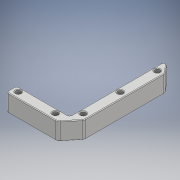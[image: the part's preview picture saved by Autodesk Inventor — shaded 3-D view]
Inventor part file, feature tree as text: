
AUTODESK INVENTOR PART (.ipt)
format: ipt  version: 2018 (Build 220112000, 112)  size: 404,992 bytes
history: native  units: mm
features: extrude x1, fillet x1, sketch x1
ambient origin geometry x8: Origin, YZ Plane, XZ Plane, XY Plane, X Axis, Y Axis, Z Axis, Center Point
bodies: Solid1 (feature_tree)
feature tree (3):
  extrude  "Extrusion1"  Depth=0.3mm
  fillet  "Fillet1"  Radius=8.0mm
  sketch  "Sketch1"  dims[d0=0.8mm d1=0.8mm d2=0.8mm d3=8.0mm d4=0.0mm d5=1.0mm d6=0.3mm]
